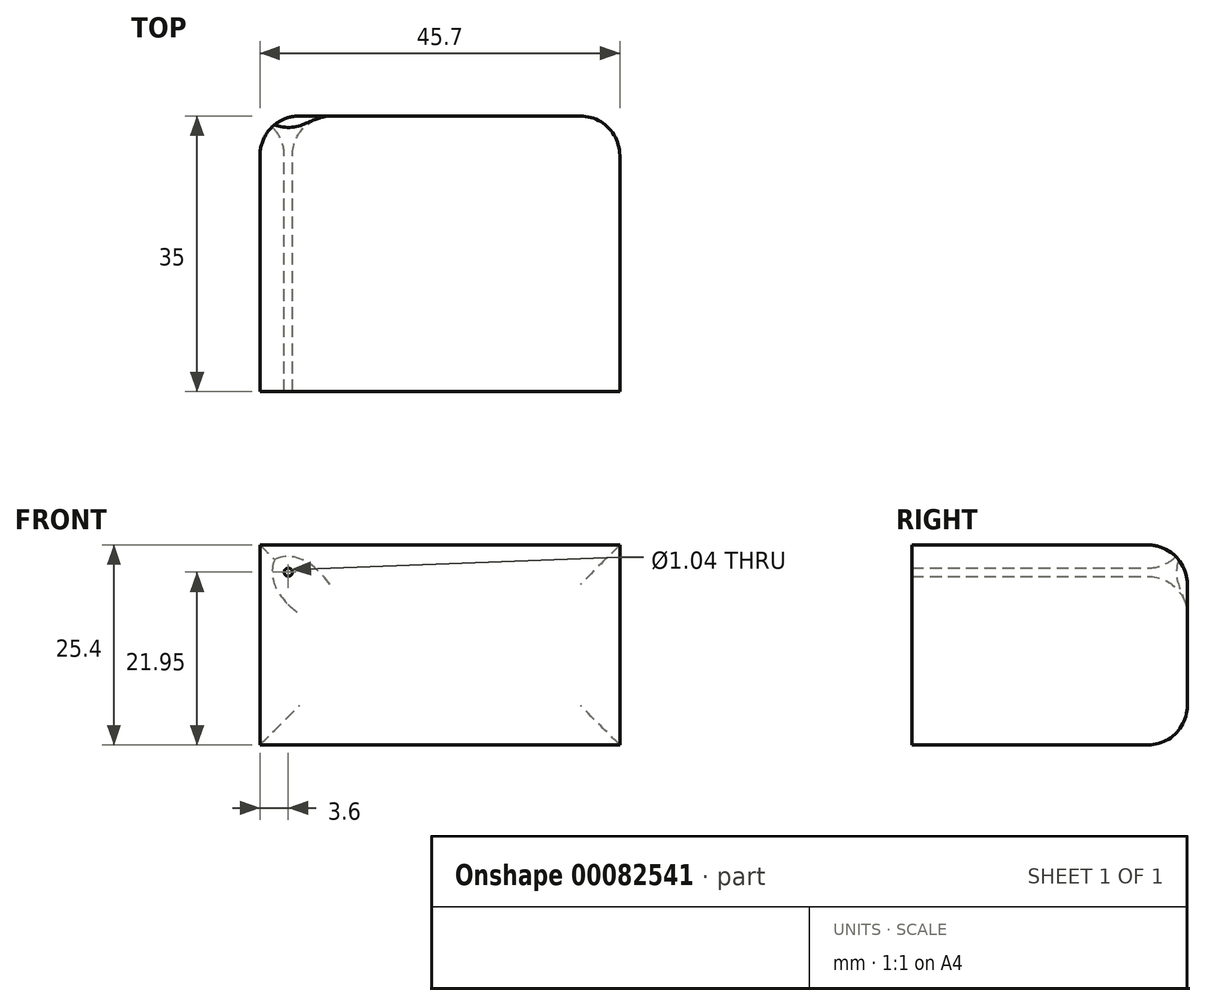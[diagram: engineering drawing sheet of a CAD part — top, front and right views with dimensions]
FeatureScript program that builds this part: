
annotation { "Feature Type Name" : "Feature", "Feature Type Description" : "" }
export const myFeature = defineFeature(function(context is Context, id is Id, definition is map)
    precondition{}
    {
        {
            var Q0;
            Q0=qCreatedBy(makeId("Front.planeOp"),FACE);
            var sketch = newSketch(context, id + "F0", { "sketchPlane" : qUnion([Q0])});
            skCircle(sketch, "E0", {"center": v(19.25, 9.25) * mm, "radius": 0.52 * mm});
            skCircle(sketch, "E1", {"center": v(19.25, 1.25) * mm, "radius": 0.52 * mm});
            skLineSegment(sketch, "E2", {"start": v(22.85, -12.7) * mm, "end": v(0, -12.7) * mm});
            skLineSegment(sketch, "E3", {"start": v(22.85, 12.7) * mm, "end": v(0, 12.7) * mm});
            skCircle(sketch, "E4.MirrorC", {"center": v(-19.25, 9.25) * mm, "radius": 0.52 * mm});
            skLineSegment(sketch, "E5.MirrorCS", {"start": v(-22.85, 12.7) * mm, "end": v(-22.85, -12.7) * mm});
            skLineSegment(sketch, "E6.MirrorCS", {"start": v(-22.85, -12.7) * mm, "end": v(0, -12.7) * mm});
            skCircle(sketch, "E7", {"center": v(-19.25, -1.5) * mm, "radius": 0.52 * mm});
            skLineSegment(sketch, "E8", {"start": v(0, 12.7) * mm, "end": v(-22.85, 12.7) * mm});
            skLineSegment(sketch, "E9", {"start": v(22.85, 12.7) * mm, "end": v(22.85, -12.7) * mm});
            skSolve(sketch);
        }
        {
            var Q0;
            Q0=makeQuery(id+"F0.imprint","IMPRINT",FACE,{"disambiguationData":[TD([[makeQuery(id+"F0.imprint","IMPRINT",EDGE,{"derivedFrom":sQuery(id+"F0.wireOp",EDGE,"E0")}),-1.0]])]});
            extrude(context, id + "F1", {"entities" : qUnion([Q0]), "depth" : 21.5 * mm});
        }
        {
            var Q0;
            Q0=makeQuery(id+"F1.opExtrude","SWEPT_EDGE",EDGE,{"disambiguationData":[OSD([sQuery(id+"F0.wireOp",EDGE,"E3"),sQuery(id+"F0.wireOp",EDGE,"E9")])]});
            fillet(context, id + "F2", {"entities" : qUnion([Q0]), "radius" : 1 * mm, "tangentPropagation" : true, "allowEdgeOverflow" : false});
        }
        {
            var Q0;
            Q0=makeQuery(id+"F1.opExtrude","SWEPT_EDGE",EDGE,{"disambiguationData":[OSD([sQuery(id+"F0.wireOp",EDGE,"E5.MirrorCS"),sQuery(id+"F0.wireOp",EDGE,"E8")])]});
            fillet(context, id + "F3", {"entities" : qUnion([Q0]), "radius" : 1 * mm, "tangentPropagation" : true, "allowEdgeOverflow" : false});
        }
        {
            var Q0;
            Q0=makeQuery(id+"F1.opExtrude","SWEPT_EDGE",EDGE,{"disambiguationData":[OSD([sQuery(id+"F0.wireOp",EDGE,"E5.MirrorCS"),sQuery(id+"F0.wireOp",EDGE,"E6.MirrorCS")])]});
            fillet(context, id + "F4", {"entities" : qUnion([Q0]), "radius" : 1 * mm, "tangentPropagation" : true, "allowEdgeOverflow" : false});
        }
        {
            var Q0;
            Q0=makeQuery(id+"F1.opExtrude","SWEPT_EDGE",EDGE,{"disambiguationData":[OSD([sQuery(id+"F0.wireOp",EDGE,"E2"),sQuery(id+"F0.wireOp",EDGE,"E9")])]});
            fillet(context, id + "F5", {"entities" : qUnion([Q0]), "radius" : 1 * mm, "tangentPropagation" : true, "allowEdgeOverflow" : false});
        }
        {
            var Q0;
            Q0=makeQuery(id+"F0.imprint","IMPRINT",FACE,{"disambiguationData":[TD([[makeQuery(id+"F0.imprint","IMPRINT",EDGE,{"derivedFrom":sQuery(id+"F0.wireOp",EDGE,"E4.MirrorC")}),-1.0]])]});
            var Q1;
            Q1=makeQuery(id+"F0.imprint","IMPRINT",FACE,{"disambiguationData":[TD([[makeQuery(id+"F0.imprint","IMPRINT",EDGE,{"derivedFrom":sQuery(id+"F0.wireOp",EDGE,"E7")}),1.0]])]});
            var Q2;
            Q2=makeQuery(id+"F0.imprint","IMPRINT",FACE,{"disambiguationData":[TD([[makeQuery(id+"F0.imprint","IMPRINT",EDGE,{"derivedFrom":sQuery(id+"F0.wireOp",EDGE,"E0")}),1.0]])]});
            var Q3;
            Q3=makeQuery(id+"F0.imprint","IMPRINT",FACE,{"disambiguationData":[TD([[makeQuery(id+"F0.imprint","IMPRINT",EDGE,{"derivedFrom":sQuery(id+"F0.wireOp",EDGE,"E1")}),1.0]])]});
            extrude(context, id + "F6", {"entities" : qUnion([Q0, Q1, Q2, Q3]), "operationType" : NewBodyOperationType.ADD, "depth" : 35 * mm});
        }
        {
            var Q0;
            Q0=makeQuery(id+"F1.opExtrude","CAP_EDGE",EDGE,{"disambiguationData":[OSD([sQuery(id+"F0.wireOp",EDGE,"E3"),sQuery(id+"F0.wireOp",EDGE,"E8")])],"isStart":true});
            var Q1;
            {var subQ0=sQuery(id+"F0.wireOp",EDGE,"E0");var subQ1=sQuery(id+"F0.wireOp",EDGE,"E1");var subQ2=sQuery(id+"F0.wireOp",EDGE,"E4.MirrorC");var subQ3=sQuery(id+"F0.wireOp",EDGE,"E7");Q1=makeQuery(id+"F6.boolean.opBoolean","MERGE",FACE,{"derivedFrom":[makeQuery(id+"F1.opExtrude","CAP_FACE",FACE,{"disambiguationData":[OSD([subQ0,subQ1,sQuery(id+"F0.wireOp",EDGE,"E2"),sQuery(id+"F0.wireOp",EDGE,"E3"),subQ2,sQuery(id+"F0.wireOp",EDGE,"E5.MirrorCS"),sQuery(id+"F0.wireOp",EDGE,"E6.MirrorCS"),subQ3,sQuery(id+"F0.wireOp",EDGE,"E8"),sQuery(id+"F0.wireOp",EDGE,"E9")])],"isStart":true}),makeQuery(id+"F6.opExtrude","CAP_FACE",FACE,{"disambiguationData":[OSD([subQ0])],"isStart":true}),makeQuery(id+"F6.opExtrude","CAP_FACE",FACE,{"disambiguationData":[OSD([subQ1])],"isStart":true}),makeQuery(id+"F6.opExtrude","CAP_FACE",FACE,{"disambiguationData":[OSD([subQ2])],"isStart":true}),makeQuery(id+"F6.opExtrude","CAP_FACE",FACE,{"disambiguationData":[OSD([subQ3])],"isStart":true})]});}
            fillet(context, id + "F7", {"entities" : qUnion([Q0, Q1]), "radius" : 5 * mm, "tangentPropagation" : true, "allowEdgeOverflow" : false});
        }
    });
